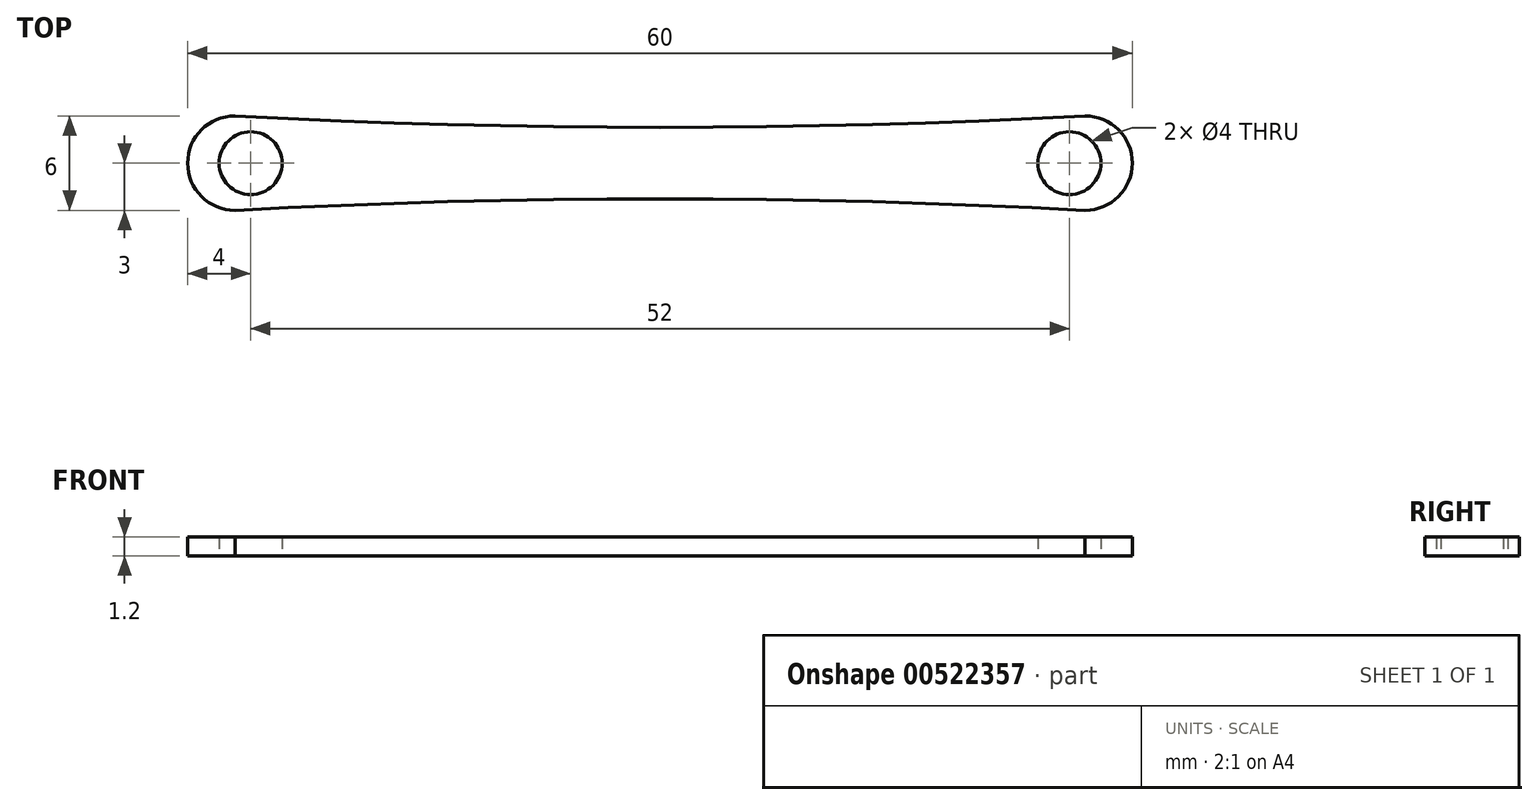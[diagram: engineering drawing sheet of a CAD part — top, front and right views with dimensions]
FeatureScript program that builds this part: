
annotation { "Feature Type Name" : "Feature", "Feature Type Description" : "" }
export const myFeature = defineFeature(function(context is Context, id is Id, definition is map)
    precondition{}
    {
        {
            var Q0;
            Q0=qCreatedBy(makeId("Top.planeOp"),FACE);
            var sketch = newSketch(context, id + "F0", { "sketchPlane" : qUnion([Q0])});
            skLineSegment(sketch, "E0.left", {"start": v(30, 0) * mm, "end": v(30, 0) * mm});
            skLineSegment(sketch, "E0.right", {"start": v(-30, 0) * mm, "end": v(-30, 0) * mm});
            skPoint(sketch, "E0.middle", {"position": v(0, 0) * mm});
            skCircle(sketch, "E1", {"center": v(-26, 0) * mm, "radius": 2 * mm});
            skLineSegment(sketch, "E2", {"start": v(0, 0) * mm, "end": v(0, -7.54) * mm, "construction": true});
            skPoint(sketch, "E2.endSnap0", {"position": v(0, -3) * mm});
            skCircle(sketch, "E3.MirrorC", {"center": v(26, 0) * mm, "radius": 2 * mm});
            skPoint(sketch, "E4.visualSharp", {"position": v(-30, 3) * mm});
            skArc(sketch, "E4.filletArc", {"start": v(-27, 3) * mm, "mid": v(-29.12, 2.12) * mm, "end": v(-30, 0) * mm});
            skPoint(sketch, "E5.visualSharp", {"position": v(-30, -3) * mm});
            skArc(sketch, "E5.filletArc", {"start": v(-30, 0) * mm, "mid": v(-29.12, -2.12) * mm, "end": v(-27, -3) * mm});
            skPoint(sketch, "E6.visualSharp", {"position": v(30, -3) * mm});
            skArc(sketch, "E6.filletArc", {"start": v(27, -3) * mm, "mid": v(29.12, -2.12) * mm, "end": v(30, 0) * mm});
            skPoint(sketch, "E7.visualSharp", {"position": v(30, 3) * mm});
            skArc(sketch, "E7.filletArc", {"start": v(30, 0) * mm, "mid": v(29.12, 2.12) * mm, "end": v(27, 3) * mm});
            skArc(sketch, "E8", {"start": v(-27, 3) * mm, "mid": v(0, 2.27) * mm, "end": v(27, 3) * mm});
            skArc(sketch, "E9", {"start": v(27, -3) * mm, "mid": v(0, -2.27) * mm, "end": v(-27, -3) * mm});
            skSolve(sketch);
        }
        {
            var Q0;
            Q0=makeQuery(id+"F0.imprint","IMPRINT",FACE,{"disambiguationData":[TD([[makeQuery(id+"F0.imprint","IMPRINT",EDGE,{"derivedFrom":sQuery(id+"F0.wireOp",EDGE,"E1")}),-1.0]])]});
            extrude(context, id + "F1", {"entities" : qUnion([Q0]), "depth" : 1.2 * mm, "offsetDistance" : 25 * mm});
        }
    });
